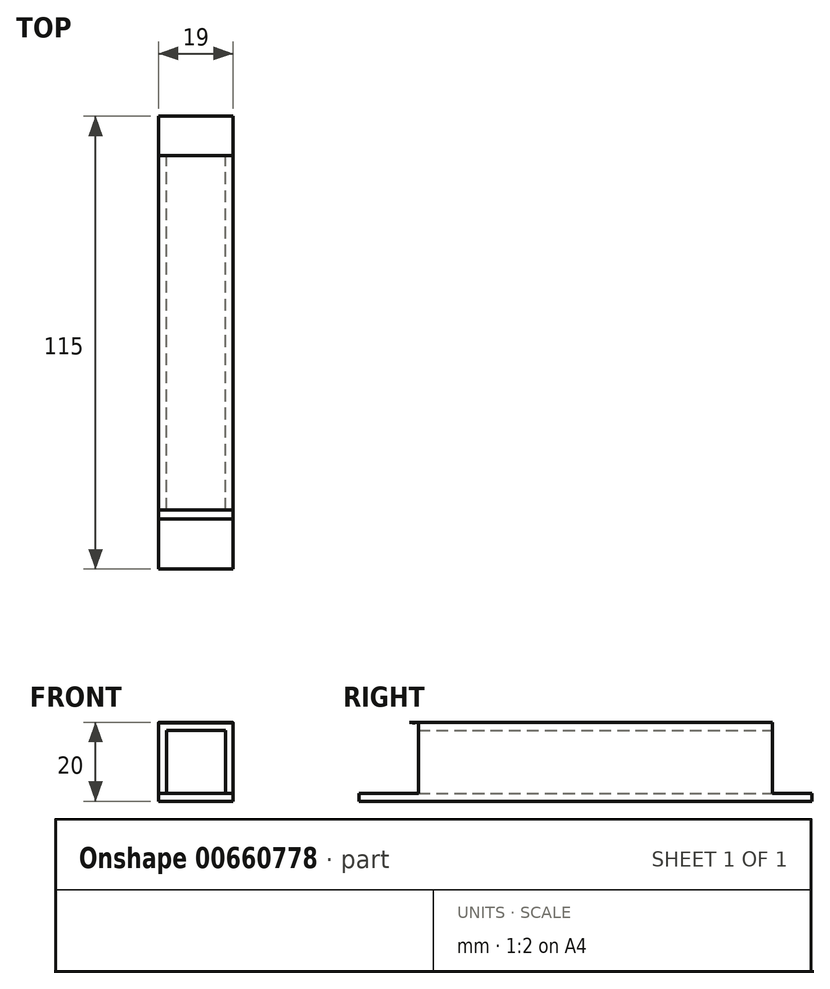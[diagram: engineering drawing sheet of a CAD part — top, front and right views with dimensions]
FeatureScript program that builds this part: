
annotation { "Feature Type Name" : "Feature", "Feature Type Description" : "" }
export const myFeature = defineFeature(function(context is Context, id is Id, definition is map)
    precondition{}
    {
        {
            var Q0;
            Q0=qCreatedBy(makeId("Right.planeOp"),FACE);
            var sketch = newSketch(context, id + "F0", { "sketchPlane" : qUnion([Q0])});
            skLineSegment(sketch, "E0.bottom", {"start": v(-45, 10) * mm, "end": v(45, 10) * mm});
            skLineSegment(sketch, "E0.top", {"start": v(-45, -10) * mm, "end": v(45, -10) * mm});
            skLineSegment(sketch, "E0.left", {"start": v(-45, 10) * mm, "end": v(-45, -10) * mm});
            skLineSegment(sketch, "E0.right", {"start": v(45, 10) * mm, "end": v(45, -10) * mm});
            skPoint(sketch, "E0.middle", {"position": v(0, 0) * mm});
            skLineSegment(sketch, "E1.bottom", {"start": v(-45, 10) * mm, "end": v(-60, 10) * mm});
            skLineSegment(sketch, "E1.left", {"start": v(-45, 10) * mm, "end": v(-45, 0) * mm});
            skLineSegment(sketch, "E2", {"start": v(-60, 10) * mm, "end": v(-60, 8) * mm});
            skLineSegment(sketch, "E3", {"start": v(-60, 8) * mm, "end": v(-45, 8) * mm});
            skLineSegment(sketch, "E4", {"start": v(-45, -10) * mm, "end": v(-60, -10) * mm});
            skLineSegment(sketch, "E5", {"start": v(-60, -10) * mm, "end": v(-60, -8) * mm});
            skLineSegment(sketch, "E6", {"start": v(-60, -8) * mm, "end": v(-45, -8) * mm});
            skLineSegment(sketch, "E7", {"start": v(45, -10) * mm, "end": v(55, -10) * mm});
            skLineSegment(sketch, "E8", {"start": v(55, -10) * mm, "end": v(55, -8) * mm});
            skLineSegment(sketch, "E9", {"start": v(55, -8) * mm, "end": v(45, -8) * mm});
            skArc(sketch, "E10", {"start": v(-55.8, 15.97) * mm, "mid": v(-51.34, 11.28) * mm, "end": v(-45, 10) * mm});
            skArc(sketch, "E11", {"start": v(-57.47, 14.03) * mm, "mid": v(-52.34, 8.73) * mm, "end": v(-45, 8) * mm});
            skSolve(sketch);
        }
        {
            var Q0;
            {var subQ5=sQuery(id+"F0.wireOp",EDGE,"E0.bottom");Q0=makeQuery(id+"F0.imprint","IMPRINT",FACE,{"disambiguationData":[TD([[makeQuery(id+"F0.imprint","IMPRINT",EDGE,{"derivedFrom":subQ5}),-1.0]])]});}
            var Q1;
            {var subQ0=sQuery(id+"F0.wireOp",EDGE,"E1.bottom");Q1=makeQuery(id+"F0.imprint","IMPRINT",FACE,{"disambiguationData":[TD([[makeQuery(id+"F0.imprint","IMPRINT",EDGE,{"derivedFrom":subQ0}),1.0]])]});}
            var Q2;
            {var subQ0=sQuery(id+"F0.wireOp",EDGE,"E4");Q2=makeQuery(id+"F0.imprint","IMPRINT",FACE,{"disambiguationData":[TD([[makeQuery(id+"F0.imprint","IMPRINT",EDGE,{"derivedFrom":subQ0}),-1.0]])]});}
            var Q3;
            {var subQ0=sQuery(id+"F0.wireOp",EDGE,"E7");Q3=makeQuery(id+"F0.imprint","IMPRINT",FACE,{"disambiguationData":[TD([[makeQuery(id+"F0.imprint","IMPRINT",EDGE,{"derivedFrom":subQ0}),1.0]])]});}
            extrude(context, id + "F1", {"entities" : qUnion([Q0, Q1, Q2, Q3]), "endBound" : BoundingType.SYMMETRIC, "depth" : 19 * mm, "offsetDistance" : 25 * mm});
        }
        {
            var Q0;
            Q0=makeQuery(id+"F1.opExtrude","SWEPT_FACE",FACE,{"disambiguationData":[OSD([sQuery(id+"F0.wireOp",EDGE,"E0.left"),sQuery(id+"F0.wireOp",EDGE,"E1.left")])]});
            var Q1;
            Q1=makeQuery(id+"F1.opExtrude","SWEPT_FACE",FACE,{"disambiguationData":[OSD([sQuery(id+"F0.wireOp",EDGE,"E0.right")])]});
            shell(context, id + "F2", {"entities" : qUnion([Q0, Q1]), "thickness" : 2 * mm});
        }
    });
